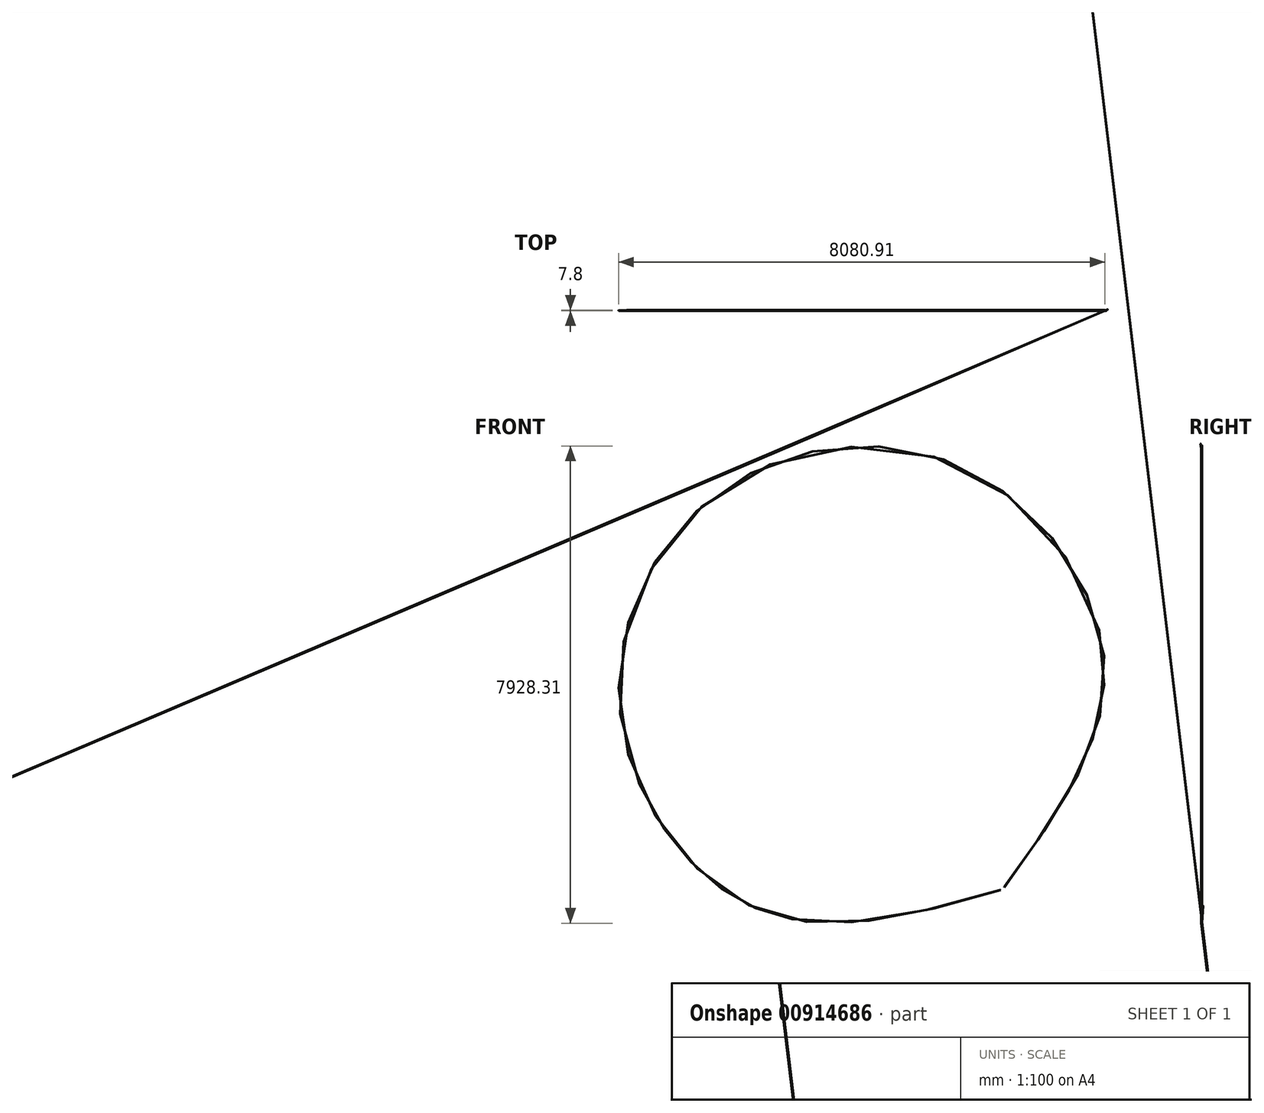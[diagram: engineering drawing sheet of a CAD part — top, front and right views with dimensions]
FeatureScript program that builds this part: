
annotation { "Feature Type Name" : "Feature", "Feature Type Description" : "" }
export const myFeature = defineFeature(function(context is Context, id is Id, definition is map)
    precondition{}
    {
        {
            var Q0;
            Q0=qCreatedBy(makeId("Top.planeOp"),FACE);
            var sketch = newSketch(context, id + "F0", { "sketchPlane" : qUnion([Q0])});
            skCircle(sketch, "E0", {"center": v(-69.26, 0) * mm, "radius": 3.62 * mm});
            skSolve(sketch);
        }
        {
            var Q0;
            Q0=qCreatedBy(makeId("Right.planeOp"),FACE);
            var sketch = newSketch(context, id + "F1", { "sketchPlane" : qUnion([Q0])});
            skCircle(sketch, "E1", {"center": v(0, 48.65) * mm, "radius": 3.9 * mm});
            skSolve(sketch);
        }
        {
            var Q0;
            Q0=qCreatedBy(makeId("Front.planeOp"),FACE);
            var sketch = newSketch(context, id + "F2", { "sketchPlane" : qUnion([Q0])});
            skArc(sketch, "E2", {"start": v(0, 48.65) * mm, "mid": v(-4683.66, 6643.1) * mm, "end": v(-69.26, 0) * mm});
            skSolve(sketch);
        }
        {
            var Q0;
            Q0=sQuery(id+"F2.wireOp",EDGE,"E2");
            var Q1;
            Q1=makeQuery(id+"F1.imprint","IMPRINT",FACE,{"disambiguationData":[TD([[makeQuery(id+"F1.imprint","IMPRINT",EDGE,{"derivedFrom":sQuery(id+"F1.wireOp",EDGE,"E1")}),1.0]])]});
            var Q2;
            Q2=makeQuery(id+"F0.imprint","IMPRINT",FACE,{"disambiguationData":[TD([[makeQuery(id+"F0.imprint","IMPRINT",EDGE,{"derivedFrom":sQuery(id+"F0.wireOp",EDGE,"E0")}),1.0]])]});
            loft(context, id + "F3", {"addSections" : true, "spine" : qUnion([Q0]), "sectionCount" : 5, "sheetProfilesArray" : [{ "sheetProfileEntities" : qUnion([Q1]) }, { "sheetProfileEntities" : qUnion([Q2]) }]});
        }
    });
